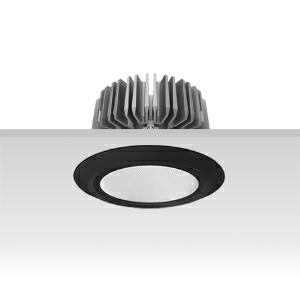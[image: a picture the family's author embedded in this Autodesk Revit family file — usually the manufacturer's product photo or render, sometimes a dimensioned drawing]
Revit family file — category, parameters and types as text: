
# Revit family: 3f_filippi_-_3f_reno_bianco_ampio_3f_filippi_-_30341_a01036_-_3f_reno_150_wh_2000-840_wide___vs_bk_a739
name_source: partatom
category: Lighting Fixtures
units: mm (PartAtom-declared; Revit-internal decimal feet)

## family parameters
Cut with Voids When Loaded = No
Host = Face
Light Source = No
Part Type = Normal
Room Calculation Point = No
Round Connector Dimension = Use Diameter
Shared = No

## types (1)
- 3F Filippi - 3F Reno Bianco Ampio (1 x LED, 1709 lm, 20 W, 4000 K)
    Apparent Load = 20 VA
    Approval mark = CE
    CIE Flux Codes = 74 93 99 100 100
    Color Rendering = 80
    Color Temperature = 4000 K
    Control Gear = Electronic ballast
    Default Elevation = 1800 mm
    Description = ILLUMINOTECHNICAL
Luminous efficiency 100% (DLOR 100%, ULOR 0%).
Initial luminous flux of the luminaire 1709 lm.
Direct symmetric wide distribution.
Installation Interdistance Transv.D = 1.12 x hu - Long.D = 1.11 x hu.
Tabular UGR (CIE 117 - 4H-8H; S=0.25H; 70/50/20): RUG 22.8 - 22.7.
Beam angle: 74° - 73°.
Luminous efficacy 85 lm/W.
Lifetime (L90/B10): 30000 h. (tq+25°C)
Lifetime (L85/B10): 50000 h. (tq+25°C)
Lifetime (L70/B10): 80000 h. (tq+25°C)
Sudden decreased luminous flux after 50000 hours: 0% (C0).
Photobiological safety in compliance with IEC/TR 62778: RG0 risk exempt, (IEC 62471).
In compliance with IEC/EN 62722-2-1 - IEC/EN 62717 standards.

SOURCE
Compact LED module 2000/840.
Energy efficiency class (UE 2019/2020 - UE 2019/2015): D.
CIE 13.3 Colour rendering index: CRI >80 (R9 <50%).
IES TM-30 Fidelity Index: Rf = 84 Rg = 95.
CCT nominal colour temperature 4000 K.
Colour initial tolerance (MacAdam): SDCM 3.
Zhaga Book 3 compliant.

MECHANICAL
Passive heat dissipator in die-casting aluminium, oversized, for optimum thermal management of the LED module.
Parabolic element with graduated/concentric rings in white polycarbonate.
Transparent external lens with glossy and satin differentiated surfaces, with a cooling and anti-insect system in methacrylate (PMMA).
Fastening spring clips in stainless steel.
Dimensions: diameter 176 mm, height 111 mm. Weight 0.8 kg.
IP44 protection degree for exposed part, IP20 for recessed part.
Mechanical strength to impacts IK06 (1 joule).
Glow-wire test resistance 650°C.

ELECTRICAL
Wiring on a separate unit.
Halogen Free electronic wiring 230V-50/60Hz, power factor 0.95, THD <25%, constant output current, SELV, class II, 1 driver.
Power of the luminaire 20 W.
ENEC - CE.
SAFE FLICKER: PstLM=<1 and SVM=<0.4 (IEC TR 61547-1 and IEC TR 63158), to ensure a more comfortable and safe light.
Luminaire compliant with EN 60598-2-22 for power supply from a centralised emergency system CPSS (Central Power Supply System), not incorporated in the luminaire - high risk areas excluded. The default power and flux are 100% in AC and 100% in DC.
Ambient temperature from 0°C to +25°C.
Temperature class T6 max 85°C.
Relative humidity UR: <85%.

INSTALLATION
Pull-up recessed fitting.
False ceiling carving: 150 mm.
All accessories dedicated to this product are available on the Catalog and on our website www.3F-Filippi.com.

ACCESSORIES
A01036 - Anti-glare microprismatic VS moulded glass, tempered, not flammable, locked and in line with the trim, in black polycarbonate.

APPLICATIONS
Environments: architectural, commercial, exhibition areas, transit areas, corridors, shops, display windows, service areas.
In false ceilings with narrow voids.

WARNING
Luminaire designed for disposal/recycling at end-of-life.
Replaceable (LED only) light source by a professional. Replaceable control gear by a professional.
    Height = 0 mm  [stored 0 ft]
    Lamp = 1 x LED
    Lamp Light Flux = 1709 lm
    Lamp Power = 20 W
    Lamp count = 1
    Length = 176 mm
    Lifetime = 50000 h
    Luminous efficacy = 85 lm/W
    Manufacturer = 3F Filippi
    ModVariant = No
    Model = 3F Filippi - 30341+A01036 - 3F Reno 150 WH 2000-840 WIDE + VS BK
    Mounting Place = Ceiling
    Mounting Type = Recessed
    Number of Poles = 1
    OnlyDefault = Yes
    Power Factor = 1
    Product Name = 3F Filippi - 3F Reno Bianco Ampio
    Product group = recessed luminaire
    ProductGroupID = 4
    Protection Class = Protection class II
    Protection Degree = IP 20
    RLX_Detail_Level = 1
    RLX_Emergency_Light_Flux = 0 lm
    RLX_Emergency_Type = 0
    RLX_Emergency_Type_DB = No
    RlxData = <blob elided: 84589 chars, md5=274e889e>
    Socket = socket
    Standby Power = 0 W
    System Light Flux = 1709 lm
    System Power = 20 W
    Type Comments = Product without accessories
    Type Image = 3ffilippi_3f_reno_150_bk_vs_smp.jpg
    URL = http://relux.com
    VarID = ---
    Voltage = 0 V
    Weight = 0.00 kg
    Width = 0 mm  [stored 0 ft]

note: [stored X ft] marks values corroborated as IEEE doubles in the binary element streams (Revit-internal decimal feet)

## geometry (parser evidence)
native form markers: Blend x4, Sweep x11
no freeform markers — native parametric forms only
